# Revit family: F-LINE-R1X115-30xxx-SI
name_source: partatom
category: Leuchten
units: mm (PartAtom-declared; Revit-internal decimal feet)

## family parameters
Basisbauteil = Fläche
Beim Laden mit Abzugskörper schneiden = Nein
Bemaßung runder Anschluss = Durchmesser verwenden
Gemeinsam genutzt = Nein
Lichtquelle = Ja
OmniClass-Nummer = 23.80.70.11
OmniClass-Titel = Luminaries for Internal Lighting
Raumberechnungspunkt = Nein
Teiletyp = Normal

## types (6) — shared parameters
Baugruppenkennzeichen = D5020200
Emissionsform beim Rendern sichtbar = Nein
Farbfilter = 16777215
Farbtemperaturverschiebung bei Dämpfen der Lampe = <Keine Auswahl>
Hersteller = RIDI Leuchten GmbH
Lampe = LED
Neigungswinkel = 90.00°
Scheinlast = 35 VA
URL = www.ridi.de
Von Breite des Rechtecks ausssenden = 1155 mm  [stored 3.78937 ft]
Von Länge des Rechtecks aussenden = 50 mm  [stored 0.164042 ft]
brand = RIDI
conformity mark = CE
electrical safety class = 1
height = 45 mm  [stored 0.147638 ft]
ingress protection (IP) code = IP20
length = 1253 mm  [stored 4.11089 ft]
nominal frequency = 50-60Hz
nominal voltage = 230
rated input power = 35
voltage type (AC, DC, UC) = AC
width = 150 mm
zero-valued in all types: Vorgabe-Ansicht

## per-type parameters (varying)
| type | Datei für fotometrisches Netz | Modell | weight |
| F-LINE-R1X115/30ND-SM-SI | F-LINE-R1x11530DA-SM.IES | 0650210SI | 3,53 |
| F-LINE-R1X115/30DA-SM-SI | F-LINE-R1x11530DA-SM.IES | 0660210SI | 3.3 |
| F-LINE-R1X115/30ND-O-SI | F-LINE-R1x11530DA-O.IES | 0650240SI | 3.7 |
| F-LINE-R1X115/30DA-O-SI | F-LINE-R1x11530DA-O.IES | 0660240SI | 3.7 |
| F-LINE-R1X115/30ND-MPS-SI | F-LINE-R1x11530DA-MPS.IES | 0650241SI | 3.7 |
| F-LINE-R1X115/30DA-MPS-SI | F-LINE-R1x11530DA-MPS.IES | 0660241SI | 3.7 |

note: column(s) folded — value = type name in every type: product name

note: [stored X ft] marks values corroborated as IEEE doubles in the binary element streams (Revit-internal decimal feet)
